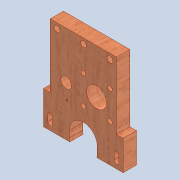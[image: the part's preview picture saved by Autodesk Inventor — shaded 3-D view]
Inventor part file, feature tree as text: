
AUTODESK INVENTOR PART (.ipt)
format: ipt  version: 2020 (Build 240168000, 168)  size: 248,320 bytes
history: native  units: mm
features: extrude x6, sketch x4, other x3, direct_edit x1, hole x1, reference x1, move_body x1
ambient origin geometry x8: Origin, YZ Plane, XZ Plane, XY Plane, X Axis, Y Axis, Z Axis, Center Point
bodies: Solid1 (feature_tree)
feature tree (17):
  extrude  "Extrusion1"  Depth=60.0mm
  extrude  "Extrusion4"  Depth=10.0mm TaperAngle=0.0deg
  extrude  "Extrusion5"  TaperAngle=0.0deg  [1 undecoded]
  extrude  "Extrusion6"  Depth=5.0mm
  extrude  "Extrusion7"  Depth=5.0mm
  extrude  "Extrusion8"  TaperAngle=0.0deg  [1 undecoded]
  direct_edit  "Direct Edit1"
  hole  "Hole1"  [1 undecoded]
  sketch  "Sketch1"  dims[d0=60.0mm d1=65.0mm]
  sketch  "Sketch7"  dims[d2=8.0mm d3=0.0mm d11=10.0mm d12=0.0mm]
  reference  "Reference6"
  sketch  "Sketch8"  dims[d13=15.0mm d14=0.0mm d15=0.0mm]
  sketch  "Sketch9"  dims[d16=0.0mm d17=0.0mm d18=5.0mm d19=5.0mm d20=0.0mm d21=0.0mm d22=5.0mm d23=3.5mm d24=5.0mm d25=10.5mm d26=7.5mm d27=30.0mm d28=25.608627mm d29=20.0mm d31=21.5mm d33=3.5mm d35=8.0mm d36=17.0mm d37=27.469095mm d38=10.0mm d39=0.0mm d42=20.0mm d43=40.0mm d44=0.0mm d45=0.0mm d46=8.0mm d47=20.0mm d48=20.0mm d49=4.0mm d50=4.5mm d51=6.0mm d52=4.0mm d53=2.0mm d54=90.0deg d55=8.0mm d56=20.594885mm]
  parser-record x1  (decoder bookkeeping rows leaked as tree rows — omitted from the tree; the rows remain in map.json)
  other  "0005-00-00 Ansamblu_General.iam"
  other  "0005-10-002 Suport1 Seringa.ipt:8"
  move_body  "Move1"
note: 3 required parameter values undecoded (feature->parameter linkage not recoverable at this tier; creation-order binding heuristic only, values carry confidence <= 0.55)
note: 1 file-system path scrubbed to <path> (originals preserved in map.json)
